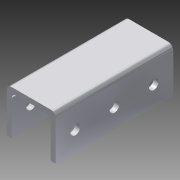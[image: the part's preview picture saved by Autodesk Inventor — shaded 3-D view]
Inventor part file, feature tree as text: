
AUTODESK INVENTOR PART (.ipt)
format: ipt  version: 2015 (Build 190159000, 159)  size: 232,960 bytes
history: native  units: in
note: dims shown in document units (in); Inventor stores cm internally (conversion verified against a paired STEP export)
features: extrude x2, sketch x2, pattern_linear x1
ambient origin geometry x8: Origin, YZ Plane, XZ Plane, XY Plane, X Axis, Y Axis, Z Axis, Center Point
bodies: Solid1 (feature_tree)
feature tree (5):
  extrude  "Extrusion1"  Depth=3.0in
  extrude  "Extrusion4"  Depth=0.5in
  pattern_linear  "Rectangular Pattern3"  Spacing1=0.0in  [1 undecoded]
  sketch  "Sketch1"  dims[d0=1.13in d1=1.25in d2=0.125in d3=0.125in d4=0.125in d5=3.0in]
  sketch  "Sketch4"  dims[d6=0.0in d35=0.5in d36=0.0in d37=0.25in d38=1.0in d39=0.0in d40=7.874in d42=1.0in d43=7.874in d45=1.0in]
note: 1 required parameter value undecoded (feature->parameter linkage not recoverable at this tier; creation-order binding heuristic only, values carry confidence <= 0.55)
